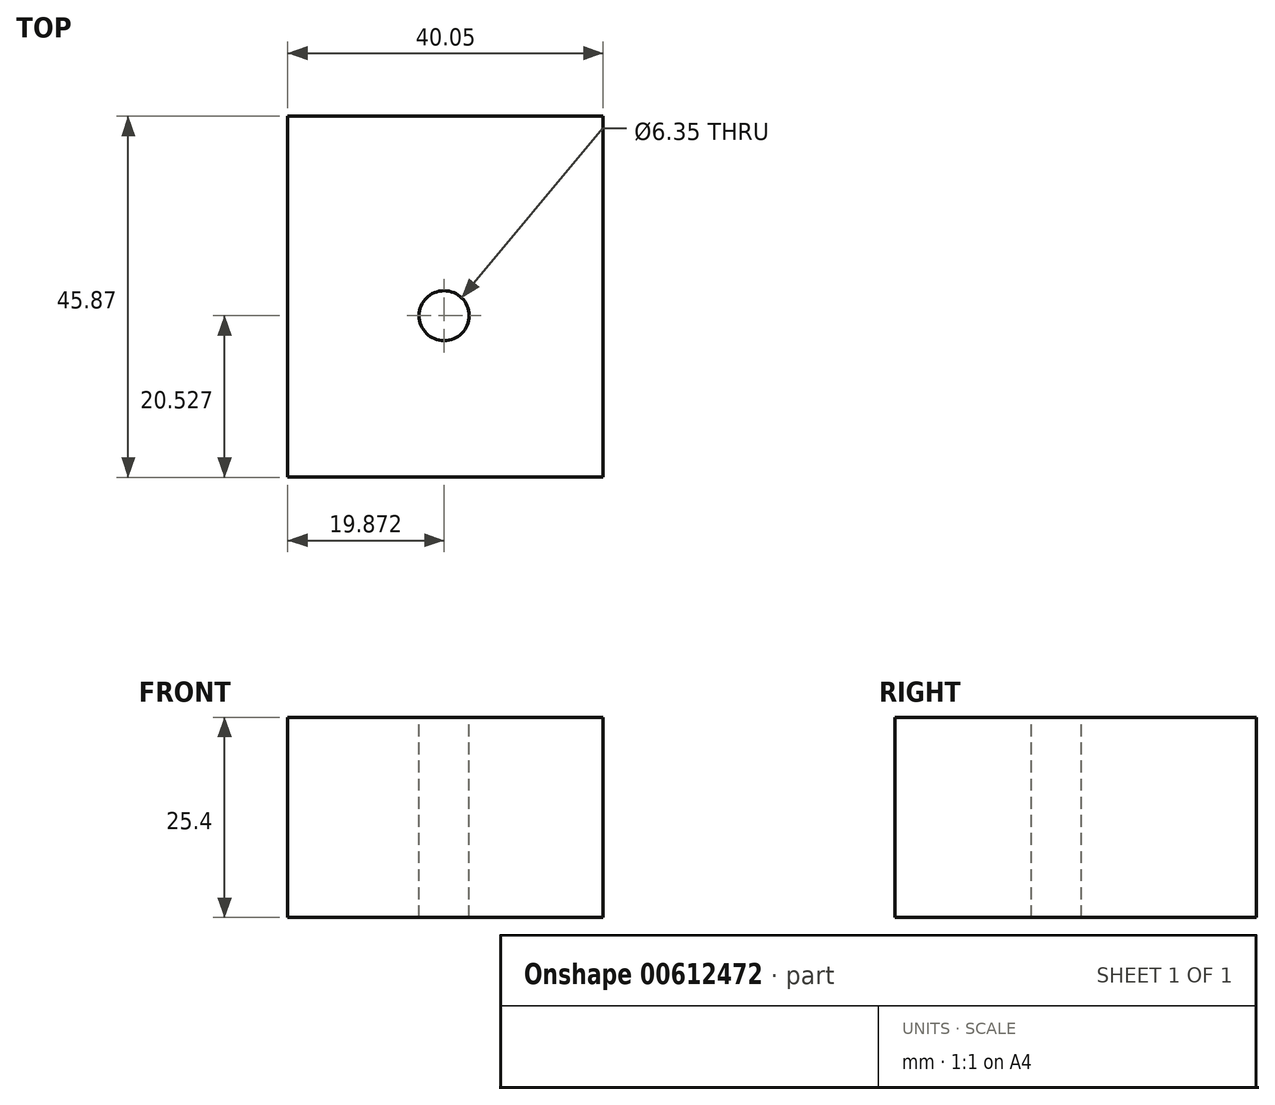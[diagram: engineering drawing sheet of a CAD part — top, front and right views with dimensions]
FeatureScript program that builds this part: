
annotation { "Feature Type Name" : "Feature", "Feature Type Description" : "" }
export const myFeature = defineFeature(function(context is Context, id is Id, definition is map)
    precondition{}
    {
        {
            var Q0;
            Q0=qCreatedBy(makeId("Top.planeOp"),FACE);
            var sketch = newSketch(context, id + "F0", { "sketchPlane" : qUnion([Q0])});
            skLineSegment(sketch, "E0.bottom", {"start": v(22.91, -26.13) * mm, "end": v(-17.14, -26.13) * mm});
            skLineSegment(sketch, "E0.top", {"start": v(22.91, 19.74) * mm, "end": v(-17.14, 19.74) * mm});
            skLineSegment(sketch, "E0.left", {"start": v(22.91, -26.13) * mm, "end": v(22.91, 19.74) * mm});
            skLineSegment(sketch, "E0.right", {"start": v(-17.14, -26.13) * mm, "end": v(-17.14, 19.74) * mm});
            skSolve(sketch);
        }
        {
            var Q0;
            Q0=makeQuery(id+"F0.imprint","IMPRINT",FACE,{"disambiguationData":[TD([[makeQuery(id+"F0.imprint","IMPRINT",EDGE,{"derivedFrom":sQuery(id+"F0.wireOp",EDGE,"E0.bottom")}),-1.0]])]});
            var sketch = newSketch(context, id + "F1", { "sketchPlane" : qUnion([Q0])});
            skSolve(sketch);
        }
        {
            var Q0;
            Q0=makeQuery(id+"F1.imprint","IMPRINT",FACE,{"disambiguationData":[TD([[makeQuery(id+"F1.imprint","IMPRINT",EDGE,{"derivedFrom":makeQuery(id+"F0.imprint","IMPRINT",EDGE,{"derivedFrom":sQuery(id+"F0.wireOp",EDGE,"E0.bottom")})}),-1.0]])]});
            extrude(context, id + "F2", {"entities" : qUnion([Q0]), "depth" : 25.4 * mm, "offsetDistance" : 25.4 * mm});
        }
        {
            var Q0;
            Q0=makeQuery(id+"F2.opExtrude","CAP_FACE",FACE,{"disambiguationData":[OSD([sQuery(id+"F0.wireOp",EDGE,"E0.bottom"),sQuery(id+"F0.wireOp",EDGE,"E0.top"),sQuery(id+"F0.wireOp",EDGE,"E0.left"),sQuery(id+"F0.wireOp",EDGE,"E0.right")])],"isStart":false});
            var sketch = newSketch(context, id + "F3", { "sketchPlane" : qUnion([Q0])});
            skPoint(sketch, "E1", {"position": v(2.73, -5.6) * mm});
            skSolve(sketch);
        }
        {
            var Q0;
            Q0=sQuery(id+"F3.wireOp",VERTEX,"E1");
            var Q1;
            Q1=makeQuery(id+"F2.opExtrude","SWEPT_BODY",BODY,{"disambiguationData":[OSD([sQuery(id+"F0.wireOp",EDGE,"E0.bottom"),sQuery(id+"F0.wireOp",EDGE,"E0.top"),sQuery(id+"F0.wireOp",EDGE,"E0.left"),sQuery(id+"F0.wireOp",EDGE,"E0.right")])]});
            hole(context, id + "F4", {"style" : HoleStyle.SIMPLE, "endStyle" : HoleEndStyle.THROUGH, "holeDiameter" : 6.35 * mm, "majorDiameter" : 6.35 * mm, "isTappedThrough" : true, "tappedDepth" : 12.7 * mm, "tapClearance" : 3, "locations" : qUnion([Q0]), "scope" : qUnion([Q1])});
        }
    });
